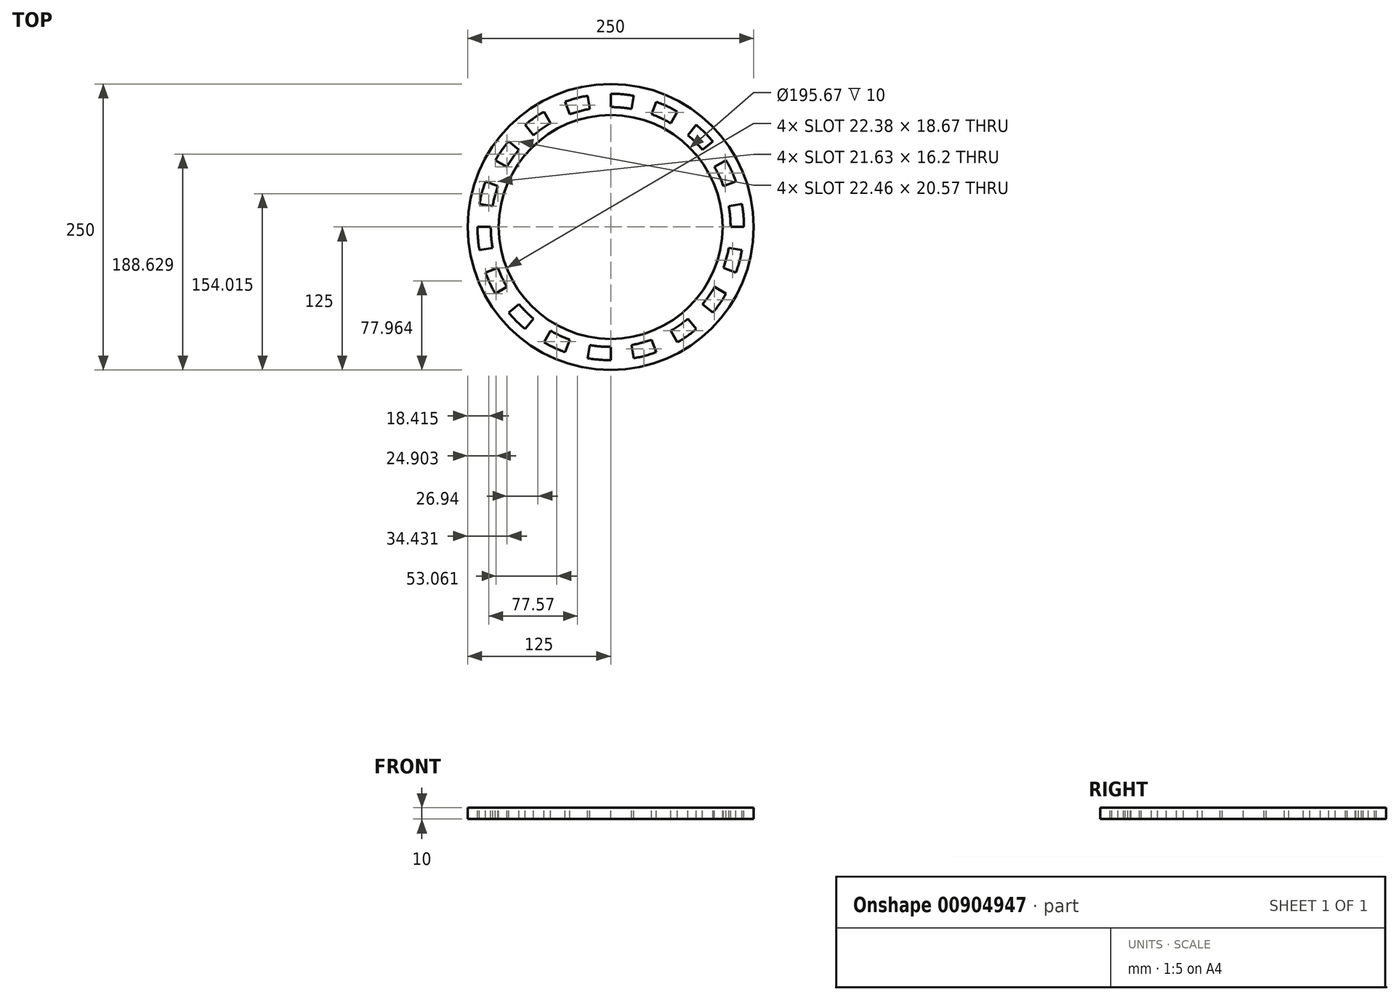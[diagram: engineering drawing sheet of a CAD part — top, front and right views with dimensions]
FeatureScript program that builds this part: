
annotation { "Feature Type Name" : "Feature", "Feature Type Description" : "" }
export const myFeature = defineFeature(function(context is Context, id is Id, definition is map)
    precondition{}
    {
        {
            var Q0;
            Q0=qCreatedBy(makeId("Top.planeOp"),FACE);
            var sketch = newSketch(context, id + "F0", { "sketchPlane" : qUnion([Q0])});
            skCircle(sketch, "E0", {"center": v(0, 0) * mm, "radius": 145 * mm});
            skArc(sketch, "E1", {"start": v(9.54, 136.41) * mm, "mid": v(4.77, 136.66) * mm, "end": v(0, 136.75) * mm});
            skArc(sketch, "E2", {"start": v(8, 114.55) * mm, "mid": v(4, 114.76) * mm, "end": v(0, 114.83) * mm});
            skLineSegment(sketch, "E3", {"start": v(0, 0) * mm, "end": v(0, 38.61) * mm, "construction": true});
            skLineSegment(sketch, "E4", {"start": v(0, 38.61) * mm, "end": v(0, 0) * mm, "construction": true});
            skLineSegment(sketch, "E5", {"start": v(0, 0) * mm, "end": v(-47.77, 0) * mm, "construction": true});
            skLineSegment(sketch, "E6", {"start": v(0, 30) * mm, "end": v(-10, 30) * mm});
            skLineSegment(sketch, "E7", {"start": v(-10, 30) * mm, "end": v(-10, 10) * mm});
            skLineSegment(sketch, "E8", {"start": v(-10, 10) * mm, "end": v(-30, 10) * mm});
            skLineSegment(sketch, "E9", {"start": v(-30, 10) * mm, "end": v(-30, 0) * mm});
            skLineSegment(sketch, "E10.MirrorCS", {"start": v(-30, -10) * mm, "end": v(-30, 0) * mm});
            skLineSegment(sketch, "E11.MirrorCS", {"start": v(-10, -10) * mm, "end": v(-30, -10) * mm});
            skLineSegment(sketch, "E12.MirrorCS", {"start": v(-10, -30) * mm, "end": v(-10, -10) * mm});
            skLineSegment(sketch, "E13.MirrorCS", {"start": v(0, -30) * mm, "end": v(-10, -30) * mm});
            skLineSegment(sketch, "E14.MirrorCS", {"start": v(0, 30) * mm, "end": v(10, 30) * mm});
            skLineSegment(sketch, "E15.MirrorCS", {"start": v(10, 30) * mm, "end": v(10, 10) * mm});
            skLineSegment(sketch, "E16.MirrorCS", {"start": v(10, 10) * mm, "end": v(30, 10) * mm});
            skLineSegment(sketch, "E17.MirrorCS", {"start": v(30, 10) * mm, "end": v(30, 0) * mm});
            skLineSegment(sketch, "E18.MirrorCS", {"start": v(30, -10) * mm, "end": v(30, 0) * mm});
            skLineSegment(sketch, "E19.MirrorCS", {"start": v(10, -10) * mm, "end": v(30, -10) * mm});
            skLineSegment(sketch, "E20.MirrorCS", {"start": v(0, -30) * mm, "end": v(10, -30) * mm});
            skLineSegment(sketch, "E21.MirrorCS", {"start": v(10, -30) * mm, "end": v(10, -10) * mm});
            skLineSegment(sketch, "E22", {"start": v(0, 114.83) * mm, "end": v(0, 136.75) * mm});
            skLineSegment(sketch, "E23", {"start": v(8, 114.55) * mm, "end": v(9.54, 136.41) * mm});
            skArc(sketch, "E24.1.0", {"start": v(-10, 114.4) * mm, "mid": v(-14, 113.98) * mm, "end": v(-17.96, 113.42) * mm});
            skLineSegment(sketch, "E24.1.1", {"start": v(-17.96, 113.42) * mm, "end": v(-21.4, 135.06) * mm});
            skArc(sketch, "E24.1.2", {"start": v(-11.92, 136.23) * mm, "mid": v(-16.67, 135.73) * mm, "end": v(-21.4, 135.06) * mm});
            skLineSegment(sketch, "E24.1.3", {"start": v(-10, 114.4) * mm, "end": v(-11.92, 136.23) * mm});
            skArc(sketch, "E24.2.0", {"start": v(-27.78, 111.42) * mm, "mid": v(-31.65, 110.39) * mm, "end": v(-35.49, 109.21) * mm});
            skLineSegment(sketch, "E24.2.1", {"start": v(-35.49, 109.21) * mm, "end": v(-42.26, 130.05) * mm});
            skArc(sketch, "E24.2.2", {"start": v(-33.08, 132.68) * mm, "mid": v(-37.7, 131.45) * mm, "end": v(-42.26, 130.05) * mm});
            skLineSegment(sketch, "E24.2.3", {"start": v(-27.78, 111.42) * mm, "end": v(-33.08, 132.68) * mm});
            skArc(sketch, "E24.3.0", {"start": v(-44.87, 105.7) * mm, "mid": v(-48.53, 104.07) * mm, "end": v(-52.13, 102.32) * mm});
            skLineSegment(sketch, "E24.3.1", {"start": v(-52.13, 102.32) * mm, "end": v(-62.08, 121.84) * mm});
            skArc(sketch, "E24.3.2", {"start": v(-53.43, 125.88) * mm, "mid": v(-57.8, 123.93) * mm, "end": v(-62.08, 121.84) * mm});
            skLineSegment(sketch, "E24.3.3", {"start": v(-44.87, 105.7) * mm, "end": v(-53.43, 125.88) * mm});
            skArc(sketch, "E24.4.0", {"start": v(-60.85, 97.38) * mm, "mid": v(-64.21, 95.2) * mm, "end": v(-67.5, 92.9) * mm});
            skLineSegment(sketch, "E24.4.1", {"start": v(-67.5, 92.9) * mm, "end": v(-80.38, 110.63) * mm});
            skArc(sketch, "E24.4.2", {"start": v(-72.47, 115.97) * mm, "mid": v(-76.47, 113.37) * mm, "end": v(-80.38, 110.63) * mm});
            skLineSegment(sketch, "E24.4.3", {"start": v(-60.85, 97.38) * mm, "end": v(-72.47, 115.97) * mm});
            skArc(sketch, "E24.5.0", {"start": v(-75.34, 86.67) * mm, "mid": v(-78.32, 83.98) * mm, "end": v(-81.2, 81.2) * mm});
            skLineSegment(sketch, "E24.5.1", {"start": v(-81.2, 81.2) * mm, "end": v(-96.7, 96.7) * mm});
            skArc(sketch, "E24.5.2", {"start": v(-89.71, 103.2) * mm, "mid": v(-93.26, 100.01) * mm, "end": v(-96.7, 96.7) * mm});
            skLineSegment(sketch, "E24.5.3", {"start": v(-75.34, 86.67) * mm, "end": v(-89.71, 103.2) * mm});
            skArc(sketch, "E24.6.0", {"start": v(-87.97, 73.81) * mm, "mid": v(-90.5, 70.7) * mm, "end": v(-92.9, 67.5) * mm});
            skLineSegment(sketch, "E24.6.1", {"start": v(-92.9, 67.5) * mm, "end": v(-110.63, 80.38) * mm});
            skArc(sketch, "E24.6.2", {"start": v(-104.75, 87.9) * mm, "mid": v(-107.76, 84.19) * mm, "end": v(-110.63, 80.38) * mm});
            skLineSegment(sketch, "E24.6.3", {"start": v(-87.97, 73.81) * mm, "end": v(-104.75, 87.9) * mm});
            skArc(sketch, "E24.7.0", {"start": v(-98.43, 59.14) * mm, "mid": v(-100.44, 55.67) * mm, "end": v(-102.32, 52.13) * mm});
            skLineSegment(sketch, "E24.7.1", {"start": v(-102.32, 52.13) * mm, "end": v(-121.84, 62.08) * mm});
            skArc(sketch, "E24.7.2", {"start": v(-117.22, 70.43) * mm, "mid": v(-119.6, 66.3) * mm, "end": v(-121.84, 62.08) * mm});
            skLineSegment(sketch, "E24.7.3", {"start": v(-98.43, 59.14) * mm, "end": v(-117.22, 70.43) * mm});
            skArc(sketch, "E24.8.0", {"start": v(-106.47, 43.02) * mm, "mid": v(-107.9, 39.28) * mm, "end": v(-109.21, 35.49) * mm});
            skLineSegment(sketch, "E24.8.1", {"start": v(-109.21, 35.49) * mm, "end": v(-130.05, 42.26) * mm});
            skArc(sketch, "E24.8.2", {"start": v(-126.79, 51.23) * mm, "mid": v(-128.5, 46.77) * mm, "end": v(-130.05, 42.26) * mm});
            skLineSegment(sketch, "E24.8.3", {"start": v(-106.47, 43.02) * mm, "end": v(-126.79, 51.23) * mm});
            skArc(sketch, "E24.9.0", {"start": v(-111.9, 25.83) * mm, "mid": v(-112.72, 21.91) * mm, "end": v(-113.42, 17.96) * mm});
            skLineSegment(sketch, "E24.9.1", {"start": v(-113.42, 17.96) * mm, "end": v(-135.06, 21.4) * mm});
            skArc(sketch, "E24.9.2", {"start": v(-133.24, 30.76) * mm, "mid": v(-134.23, 26.1) * mm, "end": v(-135.06, 21.4) * mm});
            skLineSegment(sketch, "E24.9.3", {"start": v(-111.9, 25.83) * mm, "end": v(-133.24, 30.76) * mm});
            skArc(sketch, "E24.10.0", {"start": v(-114.55, 8) * mm, "mid": v(-114.76, 4) * mm, "end": v(-114.83, 0) * mm});
            skLineSegment(sketch, "E24.10.1", {"start": v(-114.83, 0) * mm, "end": v(-136.75, 0) * mm});
            skArc(sketch, "E24.10.2", {"start": v(-136.41, 9.54) * mm, "mid": v(-136.66, 4.77) * mm, "end": v(-136.75, 0) * mm});
            skLineSegment(sketch, "E24.10.3", {"start": v(-114.55, 8) * mm, "end": v(-136.41, 9.54) * mm});
            skArc(sketch, "E24.11.0", {"start": v(-114.4, -10) * mm, "mid": v(-113.98, -14) * mm, "end": v(-113.42, -17.96) * mm});
            skLineSegment(sketch, "E24.11.1", {"start": v(-113.42, -17.96) * mm, "end": v(-135.06, -21.4) * mm});
            skArc(sketch, "E24.11.2", {"start": v(-136.23, -11.92) * mm, "mid": v(-135.73, -16.67) * mm, "end": v(-135.06, -21.4) * mm});
            skLineSegment(sketch, "E24.11.3", {"start": v(-114.4, -10) * mm, "end": v(-136.23, -11.92) * mm});
            skArc(sketch, "E24.12.0", {"start": v(-111.42, -27.78) * mm, "mid": v(-110.39, -31.65) * mm, "end": v(-109.21, -35.49) * mm});
            skLineSegment(sketch, "E24.12.1", {"start": v(-109.21, -35.49) * mm, "end": v(-130.05, -42.26) * mm});
            skArc(sketch, "E24.12.2", {"start": v(-132.68, -33.08) * mm, "mid": v(-131.45, -37.7) * mm, "end": v(-130.05, -42.26) * mm});
            skLineSegment(sketch, "E24.12.3", {"start": v(-111.42, -27.78) * mm, "end": v(-132.68, -33.08) * mm});
            skArc(sketch, "E24.13.0", {"start": v(-105.7, -44.87) * mm, "mid": v(-104.07, -48.53) * mm, "end": v(-102.32, -52.13) * mm});
            skLineSegment(sketch, "E24.13.1", {"start": v(-102.32, -52.13) * mm, "end": v(-121.84, -62.08) * mm});
            skArc(sketch, "E24.13.2", {"start": v(-125.88, -53.43) * mm, "mid": v(-123.93, -57.8) * mm, "end": v(-121.84, -62.08) * mm});
            skLineSegment(sketch, "E24.13.3", {"start": v(-105.7, -44.87) * mm, "end": v(-125.88, -53.43) * mm});
            skArc(sketch, "E24.14.0", {"start": v(-97.38, -60.85) * mm, "mid": v(-95.2, -64.21) * mm, "end": v(-92.9, -67.5) * mm});
            skLineSegment(sketch, "E24.14.1", {"start": v(-92.9, -67.5) * mm, "end": v(-110.63, -80.38) * mm});
            skArc(sketch, "E24.14.2", {"start": v(-115.97, -72.47) * mm, "mid": v(-113.37, -76.47) * mm, "end": v(-110.63, -80.38) * mm});
            skLineSegment(sketch, "E24.14.3", {"start": v(-97.38, -60.85) * mm, "end": v(-115.97, -72.47) * mm});
            skArc(sketch, "E24.15.0", {"start": v(-86.67, -75.34) * mm, "mid": v(-83.98, -78.32) * mm, "end": v(-81.2, -81.2) * mm});
            skLineSegment(sketch, "E24.15.1", {"start": v(-81.2, -81.2) * mm, "end": v(-96.7, -96.7) * mm});
            skArc(sketch, "E24.15.2", {"start": v(-103.2, -89.71) * mm, "mid": v(-100.01, -93.26) * mm, "end": v(-96.7, -96.7) * mm});
            skLineSegment(sketch, "E24.15.3", {"start": v(-86.67, -75.34) * mm, "end": v(-103.2, -89.71) * mm});
            skArc(sketch, "E24.16.0", {"start": v(-73.81, -87.97) * mm, "mid": v(-70.7, -90.5) * mm, "end": v(-67.5, -92.9) * mm});
            skLineSegment(sketch, "E24.16.1", {"start": v(-67.5, -92.9) * mm, "end": v(-80.38, -110.63) * mm});
            skArc(sketch, "E24.16.2", {"start": v(-87.9, -104.75) * mm, "mid": v(-84.19, -107.76) * mm, "end": v(-80.38, -110.63) * mm});
            skLineSegment(sketch, "E24.16.3", {"start": v(-73.81, -87.97) * mm, "end": v(-87.9, -104.75) * mm});
            skArc(sketch, "E24.17.0", {"start": v(-59.14, -98.43) * mm, "mid": v(-55.67, -100.44) * mm, "end": v(-52.13, -102.32) * mm});
            skLineSegment(sketch, "E24.17.1", {"start": v(-52.13, -102.32) * mm, "end": v(-62.08, -121.84) * mm});
            skArc(sketch, "E24.17.2", {"start": v(-70.43, -117.22) * mm, "mid": v(-66.3, -119.6) * mm, "end": v(-62.08, -121.84) * mm});
            skLineSegment(sketch, "E24.17.3", {"start": v(-59.14, -98.43) * mm, "end": v(-70.43, -117.22) * mm});
            skArc(sketch, "E24.18.0", {"start": v(-43.02, -106.47) * mm, "mid": v(-39.28, -107.9) * mm, "end": v(-35.49, -109.21) * mm});
            skLineSegment(sketch, "E24.18.1", {"start": v(-35.49, -109.21) * mm, "end": v(-42.26, -130.05) * mm});
            skArc(sketch, "E24.18.2", {"start": v(-51.23, -126.79) * mm, "mid": v(-46.77, -128.5) * mm, "end": v(-42.26, -130.05) * mm});
            skLineSegment(sketch, "E24.18.3", {"start": v(-43.02, -106.47) * mm, "end": v(-51.23, -126.79) * mm});
            skArc(sketch, "E24.19.0", {"start": v(-25.83, -111.9) * mm, "mid": v(-21.91, -112.72) * mm, "end": v(-17.96, -113.42) * mm});
            skLineSegment(sketch, "E24.19.1", {"start": v(-17.96, -113.42) * mm, "end": v(-21.4, -135.06) * mm});
            skArc(sketch, "E24.19.2", {"start": v(-30.76, -133.24) * mm, "mid": v(-26.1, -134.23) * mm, "end": v(-21.4, -135.06) * mm});
            skLineSegment(sketch, "E24.19.3", {"start": v(-25.83, -111.9) * mm, "end": v(-30.76, -133.24) * mm});
            skArc(sketch, "E24.20.0", {"start": v(-8, -114.55) * mm, "mid": v(-4, -114.76) * mm, "end": v(0, -114.83) * mm});
            skLineSegment(sketch, "E24.20.1", {"start": v(0, -114.83) * mm, "end": v(0, -136.75) * mm});
            skArc(sketch, "E24.20.2", {"start": v(-9.54, -136.41) * mm, "mid": v(-4.77, -136.66) * mm, "end": v(0, -136.75) * mm});
            skLineSegment(sketch, "E24.20.3", {"start": v(-8, -114.55) * mm, "end": v(-9.54, -136.41) * mm});
            skArc(sketch, "E24.21.0", {"start": v(10, -114.4) * mm, "mid": v(14, -113.98) * mm, "end": v(17.96, -113.42) * mm});
            skLineSegment(sketch, "E24.21.1", {"start": v(17.96, -113.42) * mm, "end": v(21.4, -135.06) * mm});
            skArc(sketch, "E24.21.2", {"start": v(11.92, -136.23) * mm, "mid": v(16.67, -135.73) * mm, "end": v(21.4, -135.06) * mm});
            skLineSegment(sketch, "E24.21.3", {"start": v(10, -114.4) * mm, "end": v(11.92, -136.23) * mm});
            skArc(sketch, "E24.22.0", {"start": v(27.78, -111.42) * mm, "mid": v(31.65, -110.39) * mm, "end": v(35.49, -109.21) * mm});
            skLineSegment(sketch, "E24.22.1", {"start": v(35.49, -109.21) * mm, "end": v(42.26, -130.05) * mm});
            skArc(sketch, "E24.22.2", {"start": v(33.08, -132.68) * mm, "mid": v(37.7, -131.45) * mm, "end": v(42.26, -130.05) * mm});
            skLineSegment(sketch, "E24.22.3", {"start": v(27.78, -111.42) * mm, "end": v(33.08, -132.68) * mm});
            skArc(sketch, "E24.23.0", {"start": v(44.87, -105.7) * mm, "mid": v(48.53, -104.07) * mm, "end": v(52.13, -102.32) * mm});
            skLineSegment(sketch, "E24.23.1", {"start": v(52.13, -102.32) * mm, "end": v(62.08, -121.84) * mm});
            skArc(sketch, "E24.23.2", {"start": v(53.43, -125.88) * mm, "mid": v(57.8, -123.93) * mm, "end": v(62.08, -121.84) * mm});
            skLineSegment(sketch, "E24.23.3", {"start": v(44.87, -105.7) * mm, "end": v(53.43, -125.88) * mm});
            skArc(sketch, "E24.24.0", {"start": v(60.85, -97.38) * mm, "mid": v(64.21, -95.2) * mm, "end": v(67.5, -92.9) * mm});
            skLineSegment(sketch, "E24.24.1", {"start": v(67.5, -92.9) * mm, "end": v(80.38, -110.63) * mm});
            skArc(sketch, "E24.24.2", {"start": v(72.47, -115.97) * mm, "mid": v(76.47, -113.37) * mm, "end": v(80.38, -110.63) * mm});
            skLineSegment(sketch, "E24.24.3", {"start": v(60.85, -97.38) * mm, "end": v(72.47, -115.97) * mm});
            skArc(sketch, "E24.25.0", {"start": v(75.34, -86.67) * mm, "mid": v(78.32, -83.98) * mm, "end": v(81.2, -81.2) * mm});
            skLineSegment(sketch, "E24.25.1", {"start": v(81.2, -81.2) * mm, "end": v(96.7, -96.7) * mm});
            skArc(sketch, "E24.25.2", {"start": v(89.71, -103.2) * mm, "mid": v(93.26, -100.01) * mm, "end": v(96.7, -96.7) * mm});
            skLineSegment(sketch, "E24.25.3", {"start": v(75.34, -86.67) * mm, "end": v(89.71, -103.2) * mm});
            skArc(sketch, "E24.26.0", {"start": v(87.97, -73.81) * mm, "mid": v(90.5, -70.7) * mm, "end": v(92.9, -67.5) * mm});
            skLineSegment(sketch, "E24.26.1", {"start": v(92.9, -67.5) * mm, "end": v(110.63, -80.38) * mm});
            skArc(sketch, "E24.26.2", {"start": v(104.75, -87.9) * mm, "mid": v(107.76, -84.19) * mm, "end": v(110.63, -80.38) * mm});
            skLineSegment(sketch, "E24.26.3", {"start": v(87.97, -73.81) * mm, "end": v(104.75, -87.9) * mm});
            skArc(sketch, "E24.27.0", {"start": v(98.43, -59.14) * mm, "mid": v(100.44, -55.67) * mm, "end": v(102.32, -52.13) * mm});
            skLineSegment(sketch, "E24.27.1", {"start": v(102.32, -52.13) * mm, "end": v(121.84, -62.08) * mm});
            skArc(sketch, "E24.27.2", {"start": v(117.22, -70.43) * mm, "mid": v(119.6, -66.3) * mm, "end": v(121.84, -62.08) * mm});
            skLineSegment(sketch, "E24.27.3", {"start": v(98.43, -59.14) * mm, "end": v(117.22, -70.43) * mm});
            skArc(sketch, "E24.28.0", {"start": v(106.47, -43.02) * mm, "mid": v(107.9, -39.28) * mm, "end": v(109.21, -35.49) * mm});
            skLineSegment(sketch, "E24.28.1", {"start": v(109.21, -35.49) * mm, "end": v(130.05, -42.26) * mm});
            skArc(sketch, "E24.28.2", {"start": v(126.79, -51.23) * mm, "mid": v(128.5, -46.77) * mm, "end": v(130.05, -42.26) * mm});
            skLineSegment(sketch, "E24.28.3", {"start": v(106.47, -43.02) * mm, "end": v(126.79, -51.23) * mm});
            skArc(sketch, "E24.29.0", {"start": v(111.9, -25.83) * mm, "mid": v(112.72, -21.91) * mm, "end": v(113.42, -17.96) * mm});
            skLineSegment(sketch, "E24.29.1", {"start": v(113.42, -17.96) * mm, "end": v(135.06, -21.4) * mm});
            skArc(sketch, "E24.29.2", {"start": v(133.24, -30.76) * mm, "mid": v(134.23, -26.1) * mm, "end": v(135.06, -21.4) * mm});
            skLineSegment(sketch, "E24.29.3", {"start": v(111.9, -25.83) * mm, "end": v(133.24, -30.76) * mm});
            skArc(sketch, "E24.30.0", {"start": v(114.55, -8) * mm, "mid": v(114.76, -4) * mm, "end": v(114.83, 0) * mm});
            skLineSegment(sketch, "E24.30.1", {"start": v(114.83, 0) * mm, "end": v(136.75, 0) * mm});
            skArc(sketch, "E24.30.2", {"start": v(136.41, -9.54) * mm, "mid": v(136.66, -4.77) * mm, "end": v(136.75, 0) * mm});
            skLineSegment(sketch, "E24.30.3", {"start": v(114.55, -8) * mm, "end": v(136.41, -9.54) * mm});
            skArc(sketch, "E24.31.0", {"start": v(114.4, 10) * mm, "mid": v(113.98, 14) * mm, "end": v(113.42, 17.96) * mm});
            skLineSegment(sketch, "E24.31.1", {"start": v(113.42, 17.96) * mm, "end": v(135.06, 21.4) * mm});
            skArc(sketch, "E24.31.2", {"start": v(136.23, 11.92) * mm, "mid": v(135.73, 16.67) * mm, "end": v(135.06, 21.4) * mm});
            skLineSegment(sketch, "E24.31.3", {"start": v(114.4, 10) * mm, "end": v(136.23, 11.92) * mm});
            skArc(sketch, "E24.32.0", {"start": v(111.42, 27.78) * mm, "mid": v(110.39, 31.65) * mm, "end": v(109.21, 35.49) * mm});
            skLineSegment(sketch, "E24.32.1", {"start": v(109.21, 35.49) * mm, "end": v(130.05, 42.26) * mm});
            skArc(sketch, "E24.32.2", {"start": v(132.68, 33.08) * mm, "mid": v(131.45, 37.7) * mm, "end": v(130.05, 42.26) * mm});
            skLineSegment(sketch, "E24.32.3", {"start": v(111.42, 27.78) * mm, "end": v(132.68, 33.08) * mm});
            skArc(sketch, "E24.33.0", {"start": v(105.7, 44.87) * mm, "mid": v(104.07, 48.53) * mm, "end": v(102.32, 52.13) * mm});
            skLineSegment(sketch, "E24.33.1", {"start": v(102.32, 52.13) * mm, "end": v(121.84, 62.08) * mm});
            skArc(sketch, "E24.33.2", {"start": v(125.88, 53.43) * mm, "mid": v(123.93, 57.8) * mm, "end": v(121.84, 62.08) * mm});
            skLineSegment(sketch, "E24.33.3", {"start": v(105.7, 44.87) * mm, "end": v(125.88, 53.43) * mm});
            skArc(sketch, "E24.34.0", {"start": v(97.38, 60.85) * mm, "mid": v(95.2, 64.21) * mm, "end": v(92.9, 67.5) * mm});
            skLineSegment(sketch, "E24.34.1", {"start": v(92.9, 67.5) * mm, "end": v(110.63, 80.38) * mm});
            skArc(sketch, "E24.34.2", {"start": v(115.97, 72.47) * mm, "mid": v(113.37, 76.47) * mm, "end": v(110.63, 80.38) * mm});
            skLineSegment(sketch, "E24.34.3", {"start": v(97.38, 60.85) * mm, "end": v(115.97, 72.47) * mm});
            skArc(sketch, "E24.35.0", {"start": v(86.67, 75.34) * mm, "mid": v(83.98, 78.32) * mm, "end": v(81.2, 81.2) * mm});
            skLineSegment(sketch, "E24.35.1", {"start": v(81.2, 81.2) * mm, "end": v(96.7, 96.7) * mm});
            skArc(sketch, "E24.35.2", {"start": v(103.2, 89.71) * mm, "mid": v(100.01, 93.26) * mm, "end": v(96.7, 96.7) * mm});
            skLineSegment(sketch, "E24.35.3", {"start": v(86.67, 75.34) * mm, "end": v(103.2, 89.71) * mm});
            skArc(sketch, "E24.36.0", {"start": v(73.81, 87.97) * mm, "mid": v(70.7, 90.5) * mm, "end": v(67.5, 92.9) * mm});
            skLineSegment(sketch, "E24.36.1", {"start": v(67.5, 92.9) * mm, "end": v(80.38, 110.63) * mm});
            skArc(sketch, "E24.36.2", {"start": v(87.9, 104.75) * mm, "mid": v(84.19, 107.76) * mm, "end": v(80.38, 110.63) * mm});
            skLineSegment(sketch, "E24.36.3", {"start": v(73.81, 87.97) * mm, "end": v(87.9, 104.75) * mm});
            skArc(sketch, "E24.37.0", {"start": v(59.14, 98.43) * mm, "mid": v(55.67, 100.44) * mm, "end": v(52.13, 102.32) * mm});
            skLineSegment(sketch, "E24.37.1", {"start": v(52.13, 102.32) * mm, "end": v(62.08, 121.84) * mm});
            skArc(sketch, "E24.37.2", {"start": v(70.43, 117.22) * mm, "mid": v(66.3, 119.6) * mm, "end": v(62.08, 121.84) * mm});
            skLineSegment(sketch, "E24.37.3", {"start": v(59.14, 98.43) * mm, "end": v(70.43, 117.22) * mm});
            skArc(sketch, "E24.38.0", {"start": v(43.02, 106.47) * mm, "mid": v(39.28, 107.9) * mm, "end": v(35.49, 109.21) * mm});
            skLineSegment(sketch, "E24.38.1", {"start": v(35.49, 109.21) * mm, "end": v(42.26, 130.05) * mm});
            skArc(sketch, "E24.38.2", {"start": v(51.23, 126.79) * mm, "mid": v(46.77, 128.5) * mm, "end": v(42.26, 130.05) * mm});
            skLineSegment(sketch, "E24.38.3", {"start": v(43.02, 106.47) * mm, "end": v(51.23, 126.79) * mm});
            skArc(sketch, "E24.39.0", {"start": v(25.83, 111.9) * mm, "mid": v(21.91, 112.72) * mm, "end": v(17.96, 113.42) * mm});
            skLineSegment(sketch, "E24.39.1", {"start": v(17.96, 113.42) * mm, "end": v(21.4, 135.06) * mm});
            skArc(sketch, "E24.39.2", {"start": v(30.76, 133.24) * mm, "mid": v(26.1, 134.23) * mm, "end": v(21.4, 135.06) * mm});
            skLineSegment(sketch, "E24.39.3", {"start": v(25.83, 111.9) * mm, "end": v(30.76, 133.24) * mm});
            skCircle(sketch, "E25", {"center": v(0, 0) * mm, "radius": 50 * mm});
            skSolve(sketch);
        }
        {
            var Q0;
            Q0=makeQuery(id+"F0.imprint","IMPRINT",FACE,{"disambiguationData":[TD([[makeQuery(id+"F0.imprint","IMPRINT",EDGE,{"derivedFrom":sQuery(id+"F0.wireOp",EDGE,"E6")}),-1.0]])]});
            extrude(context, id + "F1", {"entities" : qUnion([Q0]), "depth" : 10 * mm, "offsetDistance" : 25 * mm});
        }
        {
            var Q0;
            Q0=makeQuery(id+"F1.opExtrude","CAP_FACE",FACE,{"disambiguationData":[OSD([sQuery(id+"F0.wireOp",EDGE,"E6"),sQuery(id+"F0.wireOp",EDGE,"E7"),sQuery(id+"F0.wireOp",EDGE,"E8"),sQuery(id+"F0.wireOp",EDGE,"E9"),sQuery(id+"F0.wireOp",EDGE,"E10.MirrorCS"),sQuery(id+"F0.wireOp",EDGE,"E11.MirrorCS"),sQuery(id+"F0.wireOp",EDGE,"E12.MirrorCS"),sQuery(id+"F0.wireOp",EDGE,"E13.MirrorCS"),sQuery(id+"F0.wireOp",EDGE,"E14.MirrorCS"),sQuery(id+"F0.wireOp",EDGE,"E15.MirrorCS"),sQuery(id+"F0.wireOp",EDGE,"E16.MirrorCS"),sQuery(id+"F0.wireOp",EDGE,"E17.MirrorCS"),sQuery(id+"F0.wireOp",EDGE,"E18.MirrorCS"),sQuery(id+"F0.wireOp",EDGE,"E19.MirrorCS"),sQuery(id+"F0.wireOp",EDGE,"E20.MirrorCS"),sQuery(id+"F0.wireOp",EDGE,"E21.MirrorCS"),sQuery(id+"F0.wireOp",EDGE,"E25")])],"isStart":false});
            var sketch = newSketch(context, id + "F2", { "sketchPlane" : qUnion([Q0])});
            skCircle(sketch, "E26", {"center": v(0, 0) * mm, "radius": 125 * mm});
            skCircle(sketch, "E27", {"center": v(0, 0) * mm, "radius": 40.45 * mm});
            skSolve(sketch);
        }
        {
            var Q0;
            Q0=qSketchRegion(id+"F2",true);
            extrude(context, id + "F3", {"entities" : qUnion([Q0]), "operationType" : NewBodyOperationType.ADD, "oppositeDirection" : true, "depth" : 10 * mm, "offsetDistance" : 25 * mm});
        }
        {
            var Q0;
            Q0=makeQuery(id+"F3.boolean.opBoolean","MERGE",FACE,{"derivedFrom":[makeQuery(id+"F1.opExtrude","CAP_FACE",FACE,{"disambiguationData":[OSD([sQuery(id+"F0.wireOp",EDGE,"E6"),sQuery(id+"F0.wireOp",EDGE,"E7"),sQuery(id+"F0.wireOp",EDGE,"E8"),sQuery(id+"F0.wireOp",EDGE,"E9"),sQuery(id+"F0.wireOp",EDGE,"E10.MirrorCS"),sQuery(id+"F0.wireOp",EDGE,"E11.MirrorCS"),sQuery(id+"F0.wireOp",EDGE,"E12.MirrorCS"),sQuery(id+"F0.wireOp",EDGE,"E13.MirrorCS"),sQuery(id+"F0.wireOp",EDGE,"E14.MirrorCS"),sQuery(id+"F0.wireOp",EDGE,"E15.MirrorCS"),sQuery(id+"F0.wireOp",EDGE,"E16.MirrorCS"),sQuery(id+"F0.wireOp",EDGE,"E17.MirrorCS"),sQuery(id+"F0.wireOp",EDGE,"E18.MirrorCS"),sQuery(id+"F0.wireOp",EDGE,"E19.MirrorCS"),sQuery(id+"F0.wireOp",EDGE,"E20.MirrorCS"),sQuery(id+"F0.wireOp",EDGE,"E21.MirrorCS"),sQuery(id+"F0.wireOp",EDGE,"E25")])],"isStart":false}),makeQuery(id+"F3.opExtrude","CAP_FACE",FACE,{"disambiguationData":[OSD([sQuery(id+"F2.wireOp",EDGE,"E26"),sQuery(id+"F2.wireOp",EDGE,"E27")])],"isStart":true})]});
            var sketch = newSketch(context, id + "F4", { "sketchPlane" : qUnion([Q0])});
            skLineSegment(sketch, "E28", {"start": v(0, 104.8) * mm, "end": v(0, 116.46) * mm});
            skLineSegment(sketch, "E29", {"start": v(0, 116.46) * mm, "end": v(0, 104.8) * mm});
            skLineSegment(sketch, "E30", {"start": v(18.2, 103.21) * mm, "end": v(20.22, 114.69) * mm});
            skArc(sketch, "E31", {"start": v(20.22, 114.69) * mm, "mid": v(10.15, 116.01) * mm, "end": v(0, 116.46) * mm});
            skArc(sketch, "E32", {"start": v(18.2, 103.21) * mm, "mid": v(9.13, 104.4) * mm, "end": v(0, 104.8) * mm});
            skArc(sketch, "E33.1.0", {"start": v(-18.2, 103.21) * mm, "mid": v(-27.12, 101.23) * mm, "end": v(-35.84, 98.48) * mm});
            skLineSegment(sketch, "E33.1.1", {"start": v(-39.83, 109.43) * mm, "end": v(-35.84, 98.48) * mm});
            skArc(sketch, "E33.1.2", {"start": v(-20.22, 114.69) * mm, "mid": v(-30.14, 112.49) * mm, "end": v(-39.83, 109.43) * mm});
            skLineSegment(sketch, "E33.1.3", {"start": v(-18.2, 103.21) * mm, "end": v(-20.22, 114.69) * mm});
            skArc(sketch, "E33.2.0", {"start": v(-52.4, 90.76) * mm, "mid": v(-60.11, 85.85) * mm, "end": v(-67.37, 80.28) * mm});
            skLineSegment(sketch, "E33.2.1", {"start": v(-74.86, 89.21) * mm, "end": v(-67.37, 80.28) * mm});
            skArc(sketch, "E33.2.2", {"start": v(-58.23, 100.85) * mm, "mid": v(-66.8, 95.4) * mm, "end": v(-74.86, 89.21) * mm});
            skLineSegment(sketch, "E33.2.3", {"start": v(-52.4, 90.76) * mm, "end": v(-58.23, 100.85) * mm});
            skArc(sketch, "E33.3.0", {"start": v(-80.28, 67.37) * mm, "mid": v(-85.85, 60.11) * mm, "end": v(-90.76, 52.4) * mm});
            skLineSegment(sketch, "E33.3.1", {"start": v(-100.85, 58.23) * mm, "end": v(-90.76, 52.4) * mm});
            skArc(sketch, "E33.3.2", {"start": v(-89.21, 74.86) * mm, "mid": v(-95.4, 66.8) * mm, "end": v(-100.85, 58.23) * mm});
            skLineSegment(sketch, "E33.3.3", {"start": v(-80.28, 67.37) * mm, "end": v(-89.21, 74.86) * mm});
            skArc(sketch, "E33.4.0", {"start": v(-98.48, 35.84) * mm, "mid": v(-101.23, 27.12) * mm, "end": v(-103.21, 18.2) * mm});
            skLineSegment(sketch, "E33.4.1", {"start": v(-114.69, 20.22) * mm, "end": v(-103.21, 18.2) * mm});
            skArc(sketch, "E33.4.2", {"start": v(-109.43, 39.83) * mm, "mid": v(-112.49, 30.14) * mm, "end": v(-114.69, 20.22) * mm});
            skLineSegment(sketch, "E33.4.3", {"start": v(-98.48, 35.84) * mm, "end": v(-109.43, 39.83) * mm});
            skArc(sketch, "E33.5.0", {"start": v(-104.8, 0) * mm, "mid": v(-104.4, -9.13) * mm, "end": v(-103.21, -18.2) * mm});
            skLineSegment(sketch, "E33.5.1", {"start": v(-114.69, -20.22) * mm, "end": v(-103.21, -18.2) * mm});
            skArc(sketch, "E33.5.2", {"start": v(-116.46, 0) * mm, "mid": v(-116.01, -10.15) * mm, "end": v(-114.69, -20.22) * mm});
            skLineSegment(sketch, "E33.5.3", {"start": v(-104.8, 0) * mm, "end": v(-116.46, 0) * mm});
            skArc(sketch, "E33.6.0", {"start": v(-98.48, -35.84) * mm, "mid": v(-94.98, -44.3) * mm, "end": v(-90.76, -52.4) * mm});
            skLineSegment(sketch, "E33.6.1", {"start": v(-100.85, -58.23) * mm, "end": v(-90.76, -52.4) * mm});
            skArc(sketch, "E33.6.2", {"start": v(-109.43, -39.83) * mm, "mid": v(-105.55, -49.22) * mm, "end": v(-100.85, -58.23) * mm});
            skLineSegment(sketch, "E33.6.3", {"start": v(-98.48, -35.84) * mm, "end": v(-109.43, -39.83) * mm});
            skArc(sketch, "E33.7.0", {"start": v(-80.28, -67.37) * mm, "mid": v(-74.1, -74.1) * mm, "end": v(-67.37, -80.28) * mm});
            skLineSegment(sketch, "E33.7.1", {"start": v(-74.86, -89.21) * mm, "end": v(-67.37, -80.28) * mm});
            skArc(sketch, "E33.7.2", {"start": v(-89.21, -74.86) * mm, "mid": v(-82.35, -82.35) * mm, "end": v(-74.86, -89.21) * mm});
            skLineSegment(sketch, "E33.7.3", {"start": v(-80.28, -67.37) * mm, "end": v(-89.21, -74.86) * mm});
            skArc(sketch, "E33.8.0", {"start": v(-52.4, -90.76) * mm, "mid": v(-44.3, -94.98) * mm, "end": v(-35.84, -98.48) * mm});
            skLineSegment(sketch, "E33.8.1", {"start": v(-39.83, -109.43) * mm, "end": v(-35.84, -98.48) * mm});
            skArc(sketch, "E33.8.2", {"start": v(-58.23, -100.85) * mm, "mid": v(-49.22, -105.55) * mm, "end": v(-39.83, -109.43) * mm});
            skLineSegment(sketch, "E33.8.3", {"start": v(-52.4, -90.76) * mm, "end": v(-58.23, -100.85) * mm});
            skArc(sketch, "E33.9.0", {"start": v(-18.2, -103.21) * mm, "mid": v(-9.13, -104.4) * mm, "end": v(0, -104.8) * mm});
            skLineSegment(sketch, "E33.9.1", {"start": v(0, -116.46) * mm, "end": v(0, -104.8) * mm});
            skArc(sketch, "E33.9.2", {"start": v(-20.22, -114.69) * mm, "mid": v(-10.15, -116.01) * mm, "end": v(0, -116.46) * mm});
            skLineSegment(sketch, "E33.9.3", {"start": v(-18.2, -103.21) * mm, "end": v(-20.22, -114.69) * mm});
            skArc(sketch, "E33.10.0", {"start": v(18.2, -103.21) * mm, "mid": v(27.12, -101.23) * mm, "end": v(35.84, -98.48) * mm});
            skLineSegment(sketch, "E33.10.1", {"start": v(39.83, -109.43) * mm, "end": v(35.84, -98.48) * mm});
            skArc(sketch, "E33.10.2", {"start": v(20.22, -114.69) * mm, "mid": v(30.14, -112.49) * mm, "end": v(39.83, -109.43) * mm});
            skLineSegment(sketch, "E33.10.3", {"start": v(18.2, -103.21) * mm, "end": v(20.22, -114.69) * mm});
            skArc(sketch, "E33.11.0", {"start": v(52.4, -90.76) * mm, "mid": v(60.11, -85.85) * mm, "end": v(67.37, -80.28) * mm});
            skLineSegment(sketch, "E33.11.1", {"start": v(74.86, -89.21) * mm, "end": v(67.37, -80.28) * mm});
            skArc(sketch, "E33.11.2", {"start": v(58.23, -100.85) * mm, "mid": v(66.8, -95.4) * mm, "end": v(74.86, -89.21) * mm});
            skLineSegment(sketch, "E33.11.3", {"start": v(52.4, -90.76) * mm, "end": v(58.23, -100.85) * mm});
            skArc(sketch, "E33.12.0", {"start": v(80.28, -67.37) * mm, "mid": v(85.85, -60.11) * mm, "end": v(90.76, -52.4) * mm});
            skLineSegment(sketch, "E33.12.1", {"start": v(100.85, -58.23) * mm, "end": v(90.76, -52.4) * mm});
            skArc(sketch, "E33.12.2", {"start": v(89.21, -74.86) * mm, "mid": v(95.4, -66.8) * mm, "end": v(100.85, -58.23) * mm});
            skLineSegment(sketch, "E33.12.3", {"start": v(80.28, -67.37) * mm, "end": v(89.21, -74.86) * mm});
            skArc(sketch, "E33.13.0", {"start": v(98.48, -35.84) * mm, "mid": v(101.23, -27.12) * mm, "end": v(103.21, -18.2) * mm});
            skLineSegment(sketch, "E33.13.1", {"start": v(114.69, -20.22) * mm, "end": v(103.21, -18.2) * mm});
            skArc(sketch, "E33.13.2", {"start": v(109.43, -39.83) * mm, "mid": v(112.49, -30.14) * mm, "end": v(114.69, -20.22) * mm});
            skLineSegment(sketch, "E33.13.3", {"start": v(98.48, -35.84) * mm, "end": v(109.43, -39.83) * mm});
            skArc(sketch, "E33.14.0", {"start": v(104.8, 0) * mm, "mid": v(104.4, 9.13) * mm, "end": v(103.21, 18.2) * mm});
            skLineSegment(sketch, "E33.14.1", {"start": v(114.69, 20.22) * mm, "end": v(103.21, 18.2) * mm});
            skArc(sketch, "E33.14.2", {"start": v(116.46, 0) * mm, "mid": v(116.01, 10.15) * mm, "end": v(114.69, 20.22) * mm});
            skLineSegment(sketch, "E33.14.3", {"start": v(104.8, 0) * mm, "end": v(116.46, 0) * mm});
            skArc(sketch, "E33.15.0", {"start": v(98.48, 35.84) * mm, "mid": v(94.98, 44.3) * mm, "end": v(90.76, 52.4) * mm});
            skLineSegment(sketch, "E33.15.1", {"start": v(100.85, 58.23) * mm, "end": v(90.76, 52.4) * mm});
            skArc(sketch, "E33.15.2", {"start": v(109.43, 39.83) * mm, "mid": v(105.55, 49.22) * mm, "end": v(100.85, 58.23) * mm});
            skLineSegment(sketch, "E33.15.3", {"start": v(98.48, 35.84) * mm, "end": v(109.43, 39.83) * mm});
            skArc(sketch, "E33.16.0", {"start": v(80.28, 67.37) * mm, "mid": v(74.1, 74.1) * mm, "end": v(67.37, 80.28) * mm});
            skLineSegment(sketch, "E33.16.1", {"start": v(74.86, 89.21) * mm, "end": v(67.37, 80.28) * mm});
            skArc(sketch, "E33.16.2", {"start": v(89.21, 74.86) * mm, "mid": v(82.35, 82.35) * mm, "end": v(74.86, 89.21) * mm});
            skLineSegment(sketch, "E33.16.3", {"start": v(80.28, 67.37) * mm, "end": v(89.21, 74.86) * mm});
            skArc(sketch, "E33.17.0", {"start": v(52.4, 90.76) * mm, "mid": v(44.3, 94.98) * mm, "end": v(35.84, 98.48) * mm});
            skLineSegment(sketch, "E33.17.1", {"start": v(39.83, 109.43) * mm, "end": v(35.84, 98.48) * mm});
            skArc(sketch, "E33.17.2", {"start": v(58.23, 100.85) * mm, "mid": v(49.22, 105.55) * mm, "end": v(39.83, 109.43) * mm});
            skLineSegment(sketch, "E33.17.3", {"start": v(52.4, 90.76) * mm, "end": v(58.23, 100.85) * mm});
            skSolve(sketch);
        }
        {
            var Q0;
            Q0=qSketchRegion(id+"F4",true);
            extrude(context, id + "F5", {"entities" : qUnion([Q0]), "operationType" : NewBodyOperationType.REMOVE, "oppositeDirection" : true, "depth" : 25 * mm, "offsetDistance" : 25 * mm});
        }
        {
            var Q0;
            Q0=makeQuery(id+"F3.boolean.opBoolean","MERGE",FACE,{"derivedFrom":[makeQuery(id+"F1.opExtrude","CAP_FACE",FACE,{"disambiguationData":[OSD([sQuery(id+"F0.wireOp",EDGE,"E6"),sQuery(id+"F0.wireOp",EDGE,"E7"),sQuery(id+"F0.wireOp",EDGE,"E8"),sQuery(id+"F0.wireOp",EDGE,"E9"),sQuery(id+"F0.wireOp",EDGE,"E10.MirrorCS"),sQuery(id+"F0.wireOp",EDGE,"E11.MirrorCS"),sQuery(id+"F0.wireOp",EDGE,"E12.MirrorCS"),sQuery(id+"F0.wireOp",EDGE,"E13.MirrorCS"),sQuery(id+"F0.wireOp",EDGE,"E14.MirrorCS"),sQuery(id+"F0.wireOp",EDGE,"E15.MirrorCS"),sQuery(id+"F0.wireOp",EDGE,"E16.MirrorCS"),sQuery(id+"F0.wireOp",EDGE,"E17.MirrorCS"),sQuery(id+"F0.wireOp",EDGE,"E18.MirrorCS"),sQuery(id+"F0.wireOp",EDGE,"E19.MirrorCS"),sQuery(id+"F0.wireOp",EDGE,"E20.MirrorCS"),sQuery(id+"F0.wireOp",EDGE,"E21.MirrorCS"),sQuery(id+"F0.wireOp",EDGE,"E25")])],"isStart":false}),makeQuery(id+"F3.opExtrude","CAP_FACE",FACE,{"disambiguationData":[OSD([sQuery(id+"F2.wireOp",EDGE,"E26"),sQuery(id+"F2.wireOp",EDGE,"E27")])],"isStart":true})]});
            var sketch = newSketch(context, id + "F6", { "sketchPlane" : qUnion([Q0])});
            skCircle(sketch, "E34", {"center": v(0, 0) * mm, "radius": 97.83 * mm});
            skSolve(sketch);
        }
        {
            var Q0;
            Q0=qSketchRegion(id+"F6",true);
            extrude(context, id + "F7", {"entities" : qUnion([Q0]), "operationType" : NewBodyOperationType.REMOVE, "oppositeDirection" : true, "depth" : 25 * mm, "offsetDistance" : 25 * mm});
        }
    });
